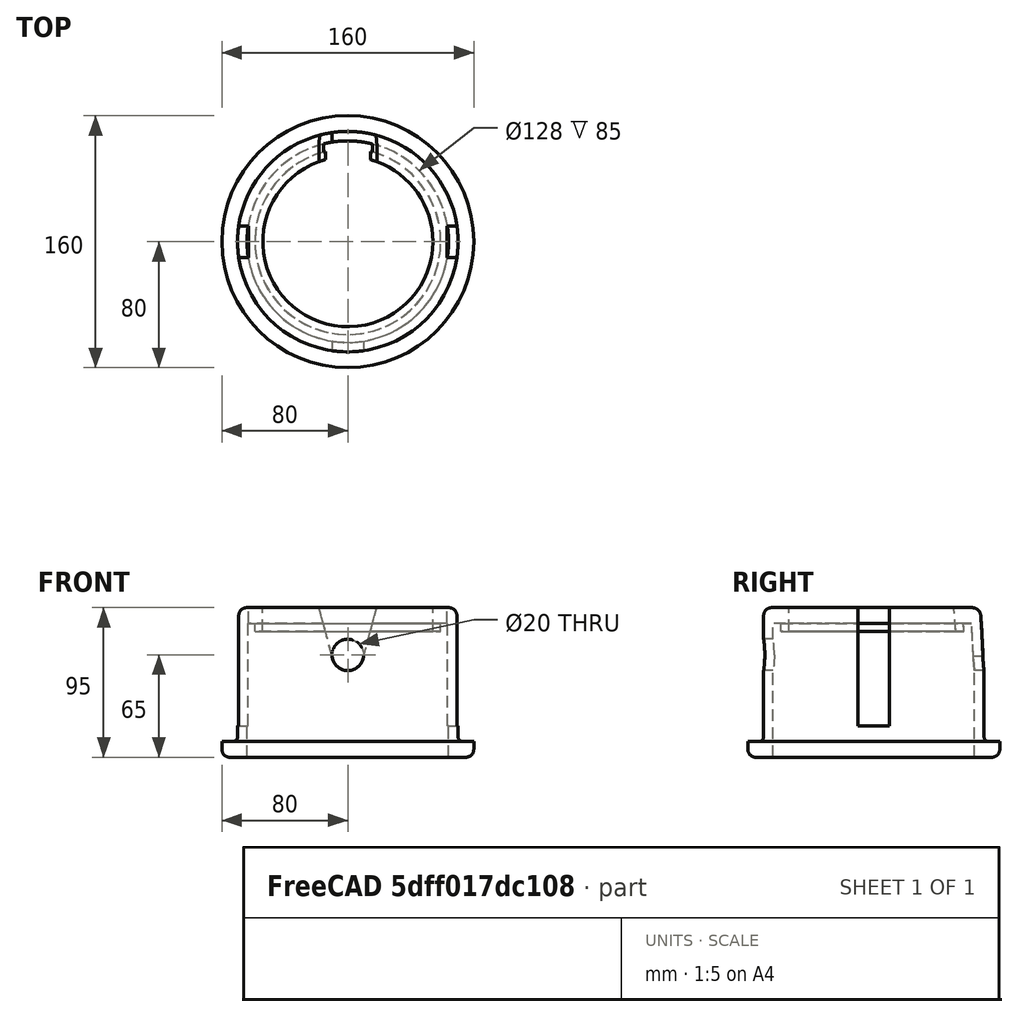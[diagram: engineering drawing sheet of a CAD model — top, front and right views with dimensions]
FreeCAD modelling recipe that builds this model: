
FCSTD DOCUMENT  (FreeCAD 0.15R4671 (Git))
Label: sphere_support_cyls4
License: All rights reserved
LicenseURL: http://en.wikipedia.org/wiki/All_rights_reserved
objects: Part::Cut×8, Part::Cylinder×6, Part::Box×5, Part::Fillet×3, Part::MultiFuse×2
note: 24 computed .brp shape members not serialized (recipe doc carries the construction recipe); baked Part::Feature solids carry a one-line shape summary decoded from their .brp

FEATURE [Part::Cylinder] Cylinder  label="Base_Cylinder"
  Angle = 360
  Height = 10
  Radius = 80
FEATURE [Part::Cylinder] Cylinder001  label="Body_Cylinder"
  Angle = 360
  Height = 90
  Placement = pos=(0,0,5) rot=(0,0,1;0rad)
  Radius = 70
FEATURE [Part::MultiFuse] Fusion  label="Core_Fusion"
  Shapes = -> [Cylinder,Cylinder001]
FEATURE [Part::Cylinder] Cylinder002  label="Inner_Hole"
  Angle = 360
  Height = 85
  Radius = 64
FEATURE [Part::Cut] Cut
  Base = -> Fusion
  Tool = -> Cylinder002
FEATURE [Part::Cylinder] Cylinder003  label="Inner_Lip"
  Angle = 360
  Height = 10
  Placement = pos=(0,0,80) rot=(0,0,1;0rad)
  Radius = 59
FEATURE [Part::MultiFuse] Fusion001
  Shapes = -> [Cut,Cylinder003]
FEATURE [Part::Cylinder] Cylinder004  label="Through_Hole"
  Angle = 360
  Height = 100
  Radius = 54
FEATURE [Part::Cut] Cut001
  Base = -> Fusion001
  Tool = -> Cylinder004
FEATURE [Part::Fillet] Fillet
  Base = -> Cut001
  Edges = 1 edges r=3: [Edge12]
FEATURE [Part::Fillet] Fillet001
  Base = -> Fillet
  Edges = 1 edges r=5: [Edge11]
FEATURE [Part::Fillet] Fillet002
  Base = -> Fillet001
  Edges = 1 edges r=5: [Edge13]
FEATURE [Part::Cylinder] Cylinder005  label="Bearing_Holes"
  Angle = 360
  Height = 180
  Placement = pos=(0,90,65) rot=(1,0,0;1.5708rad)
  Radius = 10
FEATURE [Part::Cut] Cut002
  Base = -> Fillet002
  Tool = -> Cylinder005
FEATURE [Part::Box] Box  label="Bearing_Slot"
  Height = 35
  Length = 20
  Placement = pos=(-10,48,65) rot=(0,0,1;0rad)
  Width = 25
FEATURE [Part::Cut] Cut003
  Base = -> Cut002
  Tool = -> Box
FEATURE [Part::Box] Box001  label="Cube"
  Height = 35
  Length = 10
  Placement = pos=(0,48,65) rot=(0,1,0;0.261799rad)
  Width = 25
FEATURE [Part::Cut] Cut004
  Base = -> Cut003
  Tool = -> Box001
FEATURE [Part::Box] Box002  label="Cube001"
  Height = 35
  Length = 10
  Placement = pos=(-9.95,48,64) rot=(0,-1,0;0.261799rad)
  Width = 25
FEATURE [Part::Cut] Cut005
  Base = -> Cut004
  Tool = -> Box002
FEATURE [Part::Box] Box003  label="Tab_Cut_R"
  Height = 80
  Length = 20
  Placement = pos=(63,-10,20) rot=(0,0,1;0rad)
  Width = 20
FEATURE [Part::Cut] Cut006
  Base = -> Cut005
  Tool = -> Box003
FEATURE [Part::Box] Box004  label="Tab_Cut_L"
  Height = 80
  Length = 20
  Placement = pos=(-83,-10,20) rot=(0,0,1;0rad)
  Width = 20
FEATURE [Part::Cut] Cut007
  Base = -> Cut006
  Tool = -> Box004
